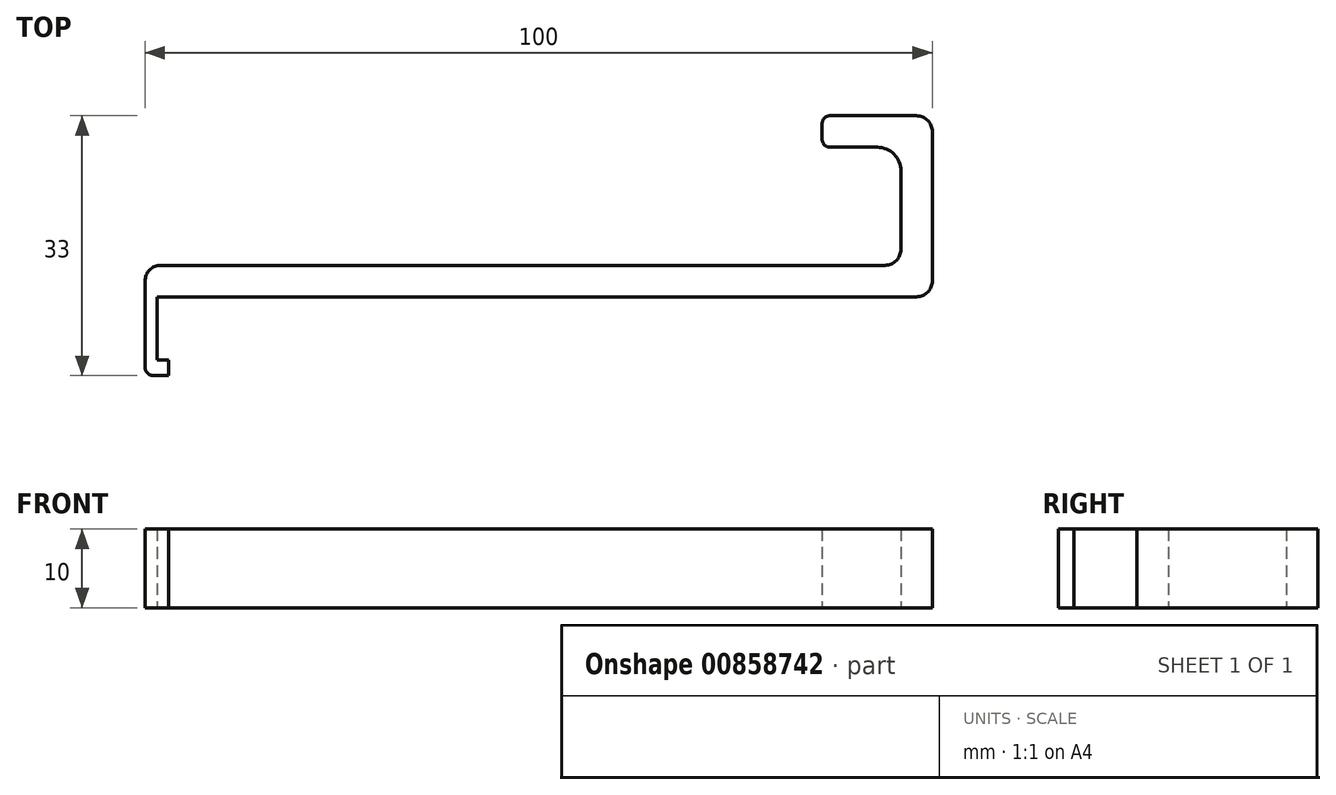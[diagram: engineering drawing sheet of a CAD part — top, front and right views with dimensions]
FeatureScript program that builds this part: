
annotation { "Feature Type Name" : "Feature", "Feature Type Description" : "" }
export const myFeature = defineFeature(function(context is Context, id is Id, definition is map)
    precondition{}
    {
        {
            var Q0;
            Q0=qCreatedBy(makeId("Top.planeOp"),FACE);
            var sketch = newSketch(context, id + "F0", { "sketchPlane" : qUnion([Q0])});
            skLineSegment(sketch, "E0", {"start": v(-23.82, 4.52) * mm, "end": v(68.18, 4.52) * mm});
            skLineSegment(sketch, "E1", {"start": v(-25.82, 2.52) * mm, "end": v(-25.82, -8.48) * mm});
            skLineSegment(sketch, "E2", {"start": v(-22.82, -9.48) * mm, "end": v(-22.82, -7.48) * mm});
            skLineSegment(sketch, "E3", {"start": v(-22.82, -7.48) * mm, "end": v(-23.32, -7.48) * mm});
            skLineSegment(sketch, "E4", {"start": v(-24.32, -6.48) * mm, "end": v(-24.32, -6.48) * mm});
            skLineSegment(sketch, "E5", {"start": v(-23.32, 0.52) * mm, "end": v(72.18, 0.52) * mm});
            skLineSegment(sketch, "E6", {"start": v(74.18, 2.52) * mm, "end": v(74.18, 21.52) * mm});
            skLineSegment(sketch, "E7", {"start": v(72.18, 23.52) * mm, "end": v(70.18, 23.52) * mm});
            skLineSegment(sketch, "E8", {"start": v(70.18, 16.52) * mm, "end": v(70.18, 6.52) * mm});
            skLineSegment(sketch, "E9", {"start": v(70.18, 23.52) * mm, "end": v(61.18, 23.52) * mm});
            skLineSegment(sketch, "E10", {"start": v(60.18, 22.52) * mm, "end": v(60.18, 20.52) * mm});
            skLineSegment(sketch, "E11", {"start": v(61.18, 19.52) * mm, "end": v(67.18, 19.52) * mm});
            skPoint(sketch, "E12.visualSharp", {"position": v(70.18, 19.52) * mm});
            skArc(sketch, "E12.filletArc", {"start": v(70.18, 16.52) * mm, "mid": v(69.3, 18.64) * mm, "end": v(67.18, 19.52) * mm});
            skPoint(sketch, "E13.visualSharp", {"position": v(60.18, 19.52) * mm});
            skArc(sketch, "E13.filletArc", {"start": v(60.18, 20.52) * mm, "mid": v(60.48, 19.81) * mm, "end": v(61.18, 19.52) * mm});
            skPoint(sketch, "E14.visualSharp", {"position": v(74.18, 23.52) * mm});
            skArc(sketch, "E14.filletArc", {"start": v(74.18, 21.52) * mm, "mid": v(73.6, 22.93) * mm, "end": v(72.18, 23.52) * mm});
            skPoint(sketch, "E15.visualSharp", {"position": v(70.18, 4.52) * mm});
            skArc(sketch, "E15.filletArc", {"start": v(68.18, 4.52) * mm, "mid": v(69.6, 5.1) * mm, "end": v(70.18, 6.52) * mm});
            skLineSegment(sketch, "E16", {"start": v(-24.82, -9.48) * mm, "end": v(-22.82, -9.48) * mm});
            skPoint(sketch, "E17.visualSharp", {"position": v(60.18, 23.52) * mm});
            skArc(sketch, "E17.filletArc", {"start": v(61.18, 23.52) * mm, "mid": v(60.48, 23.23) * mm, "end": v(60.18, 22.52) * mm});
            skPoint(sketch, "E18.visualSharp", {"position": v(-25.82, 4.52) * mm});
            skArc(sketch, "E18.filletArc", {"start": v(-23.82, 4.52) * mm, "mid": v(-25.23, 3.93) * mm, "end": v(-25.82, 2.52) * mm});
            skPoint(sketch, "E19.visualSharp", {"position": v(-24.32, 0.52) * mm});
            skPoint(sketch, "E20.visualSharp", {"position": v(-25.82, -9.48) * mm});
            skArc(sketch, "E20.filletArc", {"start": v(-25.82, -8.48) * mm, "mid": v(-25.52, -9.19) * mm, "end": v(-24.82, -9.48) * mm});
            skPoint(sketch, "E21.visualSharp", {"position": v(-24.32, -7.48) * mm});
            skPoint(sketch, "E22.visualSharp", {"position": v(74.18, 0.52) * mm});
            skArc(sketch, "E22.filletArc", {"start": v(72.18, 0.52) * mm, "mid": v(73.6, 1.1) * mm, "end": v(74.18, 2.52) * mm});
            skLineSegment(sketch, "E23", {"start": v(-23.32, 0.52) * mm, "end": v(-24.32, 0.52) * mm});
            skLineSegment(sketch, "E24", {"start": v(-24.32, -6.48) * mm, "end": v(-24.32, -7.48) * mm});
            skLineSegment(sketch, "E25", {"start": v(-23.32, -7.48) * mm, "end": v(-24.32, -7.48) * mm});
            skLineSegment(sketch, "E26", {"start": v(-24.32, -6.48) * mm, "end": v(-24.32, 0.52) * mm});
            skSolve(sketch);
        }
        {
            var Q0;
            Q0=makeQuery(id+"F0.imprint","IMPRINT",FACE,{"disambiguationData":[TD([[makeQuery(id+"F0.imprint","IMPRINT",EDGE,{"derivedFrom":sQuery(id+"F0.wireOp",EDGE,"E0")}),-1.0]])]});
            extrude(context, id + "F1", {"entities" : qUnion([Q0]), "depth" : 10 * mm, "offsetDistance" : 25 * mm});
        }
    });
